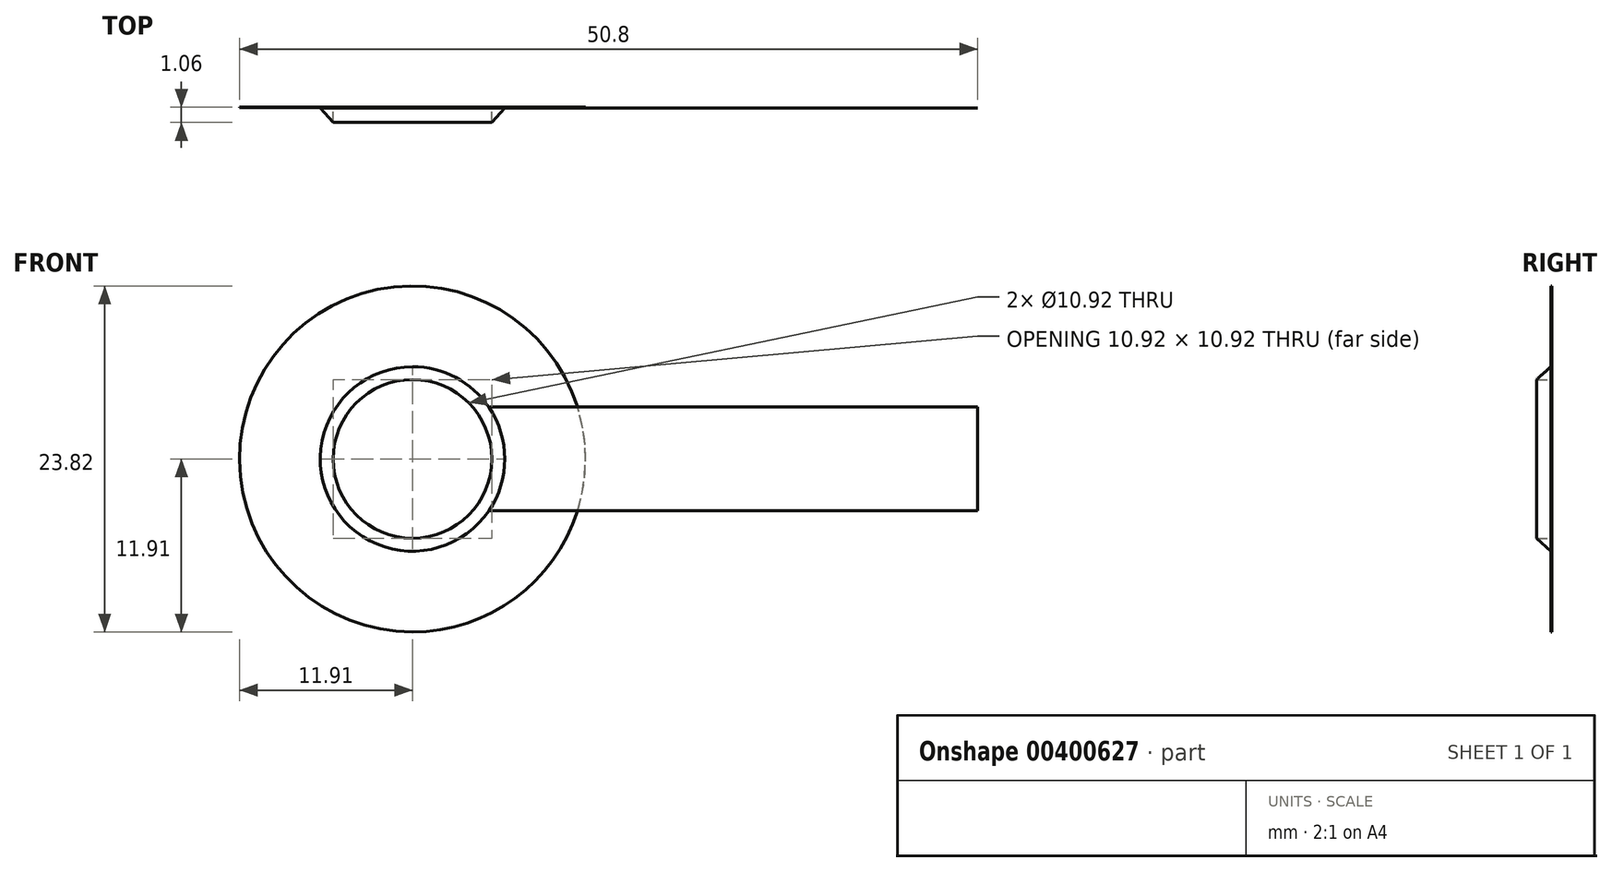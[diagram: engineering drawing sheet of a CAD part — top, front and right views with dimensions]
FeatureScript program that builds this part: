
annotation { "Feature Type Name" : "Feature", "Feature Type Description" : "" }
export const myFeature = defineFeature(function(context is Context, id is Id, definition is map)
    precondition{}
    {
        {
            var Q0;
            Q0=qCreatedBy(makeId("Front.planeOp"),FACE);
            var sketch = newSketch(context, id + "F0", { "sketchPlane" : qUnion([Q0])});
            skCircle(sketch, "E0", {"center": v(0, 0) * mm, "radius": 11.9 * mm});
            skSolve(sketch);
        }
        {
            var Q0;
            Q0 = qSketchRegion(id + "F0", true);
            extrude(context, id + "F1", {"entities" : qUnion([Q0]), "depth" : 20 / 406.4 * mm, "symmetric" : true});
        }
        {
            var Q0;
            Q0=makeQuery(id+"F1.opExtrude","CAP_FACE",FACE,{"disambiguationData":[OSD([sQuery(id+"F0.wireOp",EDGE,"E0")])],"isStart":false});
            var sketch = newSketch(context, id + "F2", { "sketchPlane" : qUnion([Q0])});
            skCircle(sketch, "E1", {"center": v(0, 0) * mm, "radius": 1.2 * mm});
            skSolve(sketch);
        }
        {
            var Q0;
            Q0 = qSketchRegion(id + "F2", true);
            extrude(context, id + "F3", {"entities" : qUnion([Q0]), "operationType" : NewBodyOperationType.ADD, "depth" : 1 / 101.6 * mm});
        }
        {
            var Q0;
            Q0=makeQuery(id+"F3.opExtrude","CAP_FACE",FACE,{"disambiguationData":[OSD([sQuery(id+"F2.wireOp",EDGE,"E1")])],"isStart":false});
            var sketch = newSketch(context, id + "F4", { "sketchPlane" : qUnion([Q0])});
            skCircle(sketch, "E2", {"center": v(0, 0) * mm, "radius": 6.35 * mm});
            skSolve(sketch);
        }
        {
            var Q0;
            Q0 = qSketchRegion(id + "F4", true);
            extrude(context, id + "F5", {"entities" : qUnion([Q0]), "operationType" : NewBodyOperationType.ADD, "depth" : 1 / 101.6 * mm});
        }
        {
            var Q0;
            Q0=makeQuery(id+"F5.opExtrude","CAP_FACE",FACE,{"disambiguationData":[OSD([sQuery(id+"F4.wireOp",EDGE,"E2")])],"isStart":false});
            var sketch = newSketch(context, id + "F6", { "sketchPlane" : qUnion([Q0])});
            skLineSegment(sketch, "E3.bottom", {"start": v(38.9, 3.57) * mm, "end": v(5.56, 3.57) * mm});
            skLineSegment(sketch, "E3.top", {"start": v(38.9, -3.57) * mm, "end": v(5.56, -3.57) * mm});
            skLineSegment(sketch, "E3.left", {"start": v(38.9, 3.57) * mm, "end": v(38.9, -3.57) * mm});
            skLineSegment(sketch, "E3.right", {"start": v(5.56, 3.57) * mm, "end": v(5.56, -3.57) * mm});
            skPoint(sketch, "E4", {"position": v(5.56, 0) * mm});
            skArc(sketch, "E5", {"start": v(5.56, 3.57) * mm, "mid": v(1.98, 0) * mm, "end": v(5.56, -3.57) * mm});
            skSolve(sketch);
        }
        {
            var Q0;
            Q0 = qSketchRegion(id + "F6", true);
            extrude(context, id + "F7", {"entities" : qUnion([Q0]), "operationType" : NewBodyOperationType.ADD, "oppositeDirection" : true, "depth" : 4 / 406.4 * mm});
        }
        {
            var Q0;
            {var subQ0=sQuery(id+"F6.wireOp",EDGE,"E5");var subQ1=sQuery(id+"F6.wireOp",EDGE,"E3.left");var subQ2=sQuery(id+"F6.wireOp",EDGE,"E3.top");var subQ3=sQuery(id+"F6.wireOp",EDGE,"E3.bottom");Q0=makeQuery(id+"FM4WlqV1iTTfunK_1.2.F7.boolean.opBoolean","MERGE",FACE,{"derivedFrom":[makeQuery(id+"FM4WlqV1iTTfunK_1.1.F7.boolean.opBoolean","MERGE",FACE,{"derivedFrom":[makeQuery(id+"F7.boolean.opBoolean","MERGE",FACE,{"derivedFrom":[makeQuery(id+"F5.opExtrude","CAP_FACE",FACE,{"disambiguationData":[OSD([sQuery(id+"F4.wireOp",EDGE,"E2")])],"isStart":false}),makeQuery(id+"F7.opExtrude","CAP_FACE",FACE,{"disambiguationData":[OSD([subQ3,subQ2,subQ1,subQ0])],"isStart":true})]}),makeQuery(id+"FM4WlqV1iTTfunK_1.1.F7.opExtrude","CAP_FACE",FACE,{"disambiguationData":[OSD([subQ3,subQ2,subQ1,subQ0])],"isStart":true})]}),makeQuery(id+"FM4WlqV1iTTfunK_1.2.F7.opExtrude","CAP_FACE",FACE,{"disambiguationData":[OSD([subQ3,subQ2,subQ1,subQ0])],"isStart":true})]});}
            cPlane(context, id + "F8", {"entities" : qUnion([Q0]), "cplaneType" : CPlaneType.OFFSET, "offset" : 6.35 * mm, "width" : 152.4 * mm, "height" : 152.4 * mm});
        }
        {
            var Q0;
            Q0=qCreatedBy(id+"F8.planeOp",FACE);
            var sketch = newSketch(context, id + "F9", { "sketchPlane" : qUnion([Q0])});
            skCircle(sketch, "E6", {"center": v(0, 0) * mm, "radius": 0.67 * mm});
            skSolve(sketch);
        }
        {
            var Q0;
            {var subQ0=sQuery(id+"F6.wireOp",EDGE,"E5");var subQ1=sQuery(id+"F6.wireOp",EDGE,"E3.left");var subQ2=sQuery(id+"F6.wireOp",EDGE,"E3.top");var subQ3=sQuery(id+"F6.wireOp",EDGE,"E3.bottom");Q0=makeQuery(id+"FM4WlqV1iTTfunK_1.2.F7.boolean.opBoolean","MERGE",FACE,{"derivedFrom":[makeQuery(id+"FM4WlqV1iTTfunK_1.1.F7.boolean.opBoolean","MERGE",FACE,{"derivedFrom":[makeQuery(id+"F7.boolean.opBoolean","MERGE",FACE,{"derivedFrom":[makeQuery(id+"F5.opExtrude","CAP_FACE",FACE,{"disambiguationData":[OSD([sQuery(id+"F4.wireOp",EDGE,"E2")])],"isStart":false}),makeQuery(id+"F7.opExtrude","CAP_FACE",FACE,{"disambiguationData":[OSD([subQ3,subQ2,subQ1,subQ0])],"isStart":true})]}),makeQuery(id+"FM4WlqV1iTTfunK_1.1.F7.opExtrude","CAP_FACE",FACE,{"disambiguationData":[OSD([subQ3,subQ2,subQ1,subQ0])],"isStart":true})]}),makeQuery(id+"FM4WlqV1iTTfunK_1.2.F7.opExtrude","CAP_FACE",FACE,{"disambiguationData":[OSD([subQ3,subQ2,subQ1,subQ0])],"isStart":true})]});}
            var sketch = newSketch(context, id + "F10", { "sketchPlane" : qUnion([Q0])});
            skCircle(sketch, "E7", {"center": v(0, 0) * mm, "radius": 6.35 * mm});
            skSolve(sketch);
        }
        {
            var Q1;
            Q1 = qSketchRegion(id + "F10", true);
            var Q2;
            Q2 = qSketchRegion(id + "F9", true);
            loft(context, id + "F11", {"operationType" : NewBodyOperationType.ADD, "sheetProfilesArray" : [{ "sheetProfileEntities" : qUnion([Q1]) }, { "sheetProfileEntities" : qUnion([Q2]) }]});
        }
        {
            var Q0;
            Q0=makeQuery(id+"F1.opExtrude","CAP_FACE",FACE,{"disambiguationData":[OSD([sQuery(id+"F0.wireOp",EDGE,"E0")])],"isStart":true});
            var sketch = newSketch(context, id + "F12", { "sketchPlane" : qUnion([Q0])});
            skCircle(sketch, "E8", {"center": v(0, 0) * mm, "radius": 5.46 * mm});
            skSolve(sketch);
        }
        {
            var Q0;
            Q0 = qSketchRegion(id + "F12", true);
            extrude(context, id + "F13", {"entities" : qUnion([Q0]), "operationType" : NewBodyOperationType.REMOVE, "oppositeDirection" : true, "depth" : 20 * mm});
        }
    });
